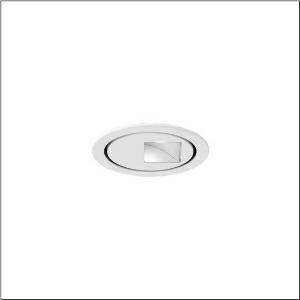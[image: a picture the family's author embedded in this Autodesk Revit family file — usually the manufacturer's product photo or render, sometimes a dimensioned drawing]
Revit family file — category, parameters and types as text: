
# Revit family: lunis_11_micro_round_51dj11b71wf21
name_source: partatom
category: Lighting Fixtures
units: mm (PartAtom-declared; Revit-internal decimal feet)

## family parameters
Cut with Voids When Loaded = No
Host = Face
Light Source = No
Part Type = Normal
Room Calculation Point = No
Round Connector Dimension = Use Diameter
Shared = No

## types (1)
- Lunis 11 micro round (1 x LED 3000K / CRI = 80 (unbekannt), 1320 lm, 3000K)
    Apparent Load = 20 VA
    CIE Flux Codes = 42 75 96 100 100
    Color Rendering = 80
    Color Temperature = 3000K
    Default Elevation = 1800 mm
    Description = Lunis 11 micro round, downlight, light control with wallwasher, of highly reflective aluminium, highly specular, light emission: direct distribution, LED rated luminous flux: 1.320lm, light colour: 830, with terminal, 3-pole, mains connection: 220..230V, AC, 50/60Hz, LED module, of aluminium, highly specular, white, diameter: 114mm, clamping range: 1..40mm, recessing ring, of plastic, traffic white (RAL 9016), protection rating (complete): IP20, insulation class (complete): insulation class II (safety insulation), certification: CE, permissible ambient temperature for indoor applications: 0..+35°C, packaging unit: 1 piece
    Height = 0 mm  [stored 0 ft]
    Lamp = 1 x LED 3000K / CRI >= 80 (unbekannt)
    Lamp Light Flux = 1320 lm
    Lamp count = 1
    Length = 114 mm
    Luminous efficacy = 67 lm/W
    Manufacturer = Siteco
    ModVariant = No
    Model = 51DJ11B71WF21
    Mounting Place = Ceiling
    Mounting Type = Recessed
    Number of Poles = 1
    OnlyDefault = Yes
    Power Factor = 1
    Product Name = Lunis 11 micro round
    Product group = downlight
    ProductGroupID = 400
    Protection Class = Protection class II
    Protection Degree = IP 20
    RLX_Detail_Level = 1
    RLX_Emergency_Light_Flux = 0 lm
    RLX_Emergency_Type = 0
    RLX_Emergency_Type_DB = No
    RlxData = <blob elided: 40801 chars, md5=80ba3915>
    Socket = socket
    Standby Power = 0 W
    System Light Flux = 1320 lm
    System Power = 20 W
    Type Comments = Product without accessories
    Type Image = l_1004773.jpg
    URL = http://relux.com
    VarID = ---
    Voltage = 0 V
    Weight = 0.00 kg
    Width = 114 mm

note: [stored X ft] marks values corroborated as IEEE doubles in the binary element streams (Revit-internal decimal feet)

## geometry (parser evidence)
native form markers: Blend x4, Sweep x10
no freeform markers — native parametric forms only
